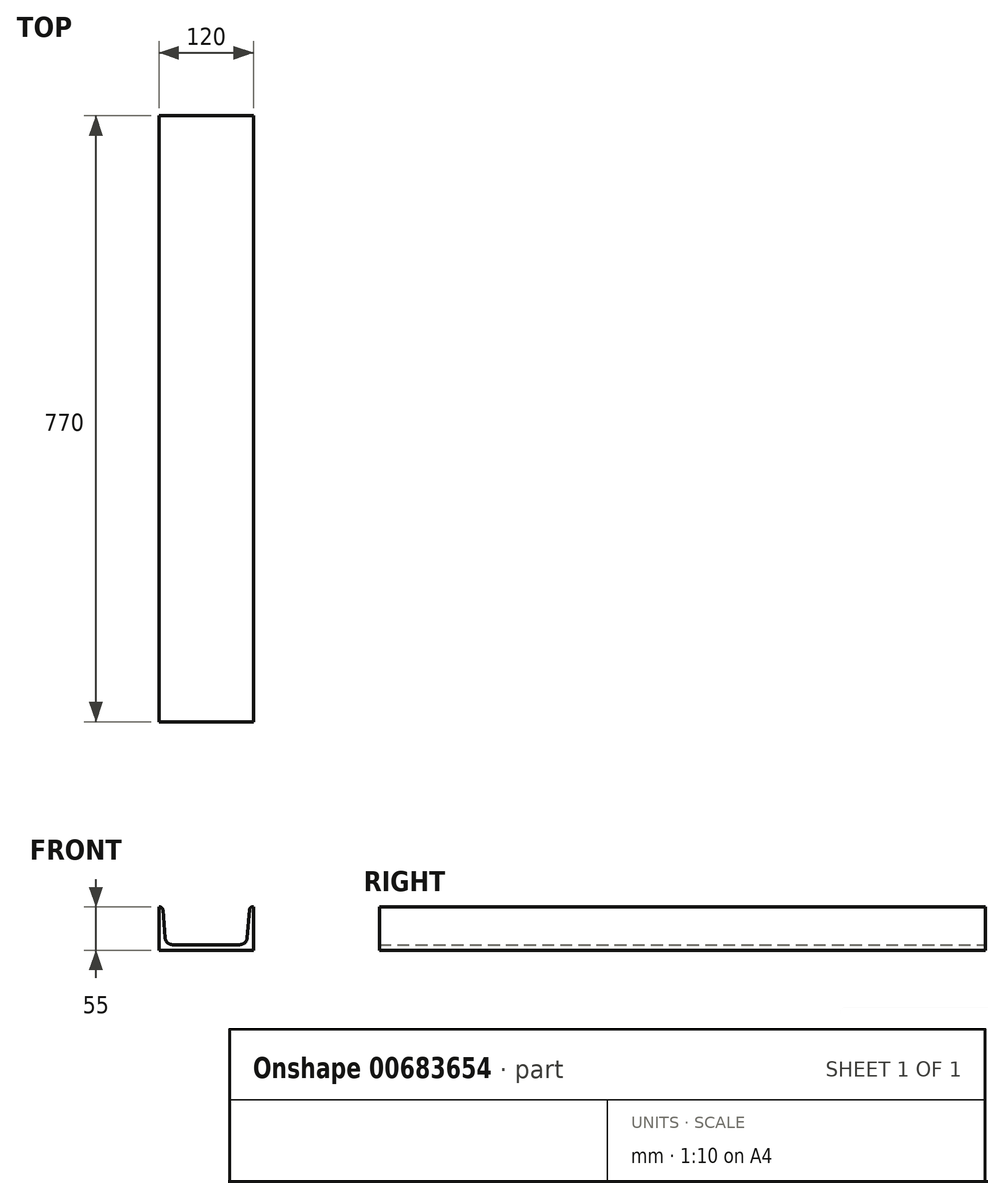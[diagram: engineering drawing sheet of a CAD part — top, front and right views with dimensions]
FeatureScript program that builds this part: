
annotation { "Feature Type Name" : "Feature", "Feature Type Description" : "" }
export const myFeature = defineFeature(function(context is Context, id is Id, definition is map)
    precondition{}
    {
        {
            var Q0;
            Q0=qCreatedBy(makeId("Front.planeOp"),FACE);
            var sketch = newSketch(context, id + "F0", { "sketchPlane" : qUnion([Q0])});
            skLineSegment(sketch, "E0", {"start": v(0, 55) * mm, "end": v(0, 0) * mm});
            skLineSegment(sketch, "E1", {"start": v(0, 0) * mm, "end": v(120, 0) * mm});
            skLineSegment(sketch, "E2", {"start": v(120, 0) * mm, "end": v(120, 55) * mm});
            skLineSegment(sketch, "E3.0", {"start": v(16.95, 7) * mm, "end": v(103.05, 7) * mm});
            skLineSegment(sketch, "E4", {"start": v(7.98, 15.28) * mm, "end": v(5.13, 50.86) * mm});
            skLineSegment(sketch, "E5", {"start": v(0, 55) * mm, "end": v(0.65, 55) * mm});
            skArc(sketch, "E6.filletArc", {"start": v(7.98, 15.28) * mm, "mid": v(10.84, 9.39) * mm, "end": v(16.95, 7) * mm});
            skPoint(sketch, "E7.visualSharp", {"position": v(4.8, 55) * mm});
            skArc(sketch, "E7.filletArc", {"start": v(5.13, 50.86) * mm, "mid": v(3.7, 53.8) * mm, "end": v(0.65, 55) * mm});
            skLineSegment(sketch, "E8", {"start": v(60, 0) * mm, "end": v(60, 20.87) * mm, "construction": true});
            skArc(sketch, "E9.MirrorCS", {"start": v(112.02, 15.28) * mm, "mid": v(109.16, 9.39) * mm, "end": v(103.05, 7) * mm});
            skLineSegment(sketch, "E10.MirrorCS", {"start": v(112.02, 15.28) * mm, "end": v(114.87, 50.86) * mm});
            skArc(sketch, "E11.MirrorCS", {"start": v(114.87, 50.86) * mm, "mid": v(116.3, 53.8) * mm, "end": v(119.35, 55) * mm});
            skLineSegment(sketch, "E12.MirrorCS", {"start": v(120, 55) * mm, "end": v(119.35, 55) * mm});
            skSolve(sketch);
        }
        {
            var Q0;
            Q0=makeQuery(id+"F0.imprint","IMPRINT",FACE,{"disambiguationData":[TD([[makeQuery(id+"F0.imprint","IMPRINT",EDGE,{"derivedFrom":sQuery(id+"F0.wireOp",EDGE,"E0")}),1.0]])]});
            extrude(context, id + "F1", {"entities" : qUnion([Q0]), "depth" : 770 * mm, "offsetDistance" : 25 * mm});
        }
    });
